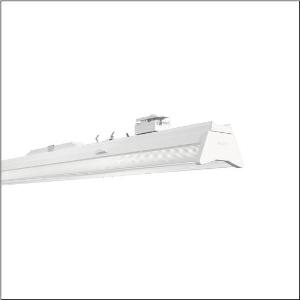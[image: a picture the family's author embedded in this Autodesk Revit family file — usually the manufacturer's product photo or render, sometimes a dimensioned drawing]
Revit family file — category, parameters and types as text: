
# Revit family: licross_r__11_performance_tw_51tm16tnt45x_2116
name_source: partatom
category: Lighting Fixtures
units: mm (PartAtom-declared; Revit-internal decimal feet)

## family parameters
Cut with Voids When Loaded = No
Host = Face
Light Source = No
Part Type = Normal
Room Calculation Point = No
Round Connector Dimension = Use Diameter
Shared = No

## types (1)
- --- (1 x LED 2700 K ... 6500 K, 4700 lm, 28.9 W, 2700K)
    Apparent Load = 29 VA
    CIE Flux Codes = 63 87 95 78 100
    Color Rendering = 80
    Color Temperature = 2700K
    Default Elevation = 1800 mm
    Description = Licross® 11 Performance TW, luminaire insert, of sheet steel, galvanised, coil coated, white, length: 1.500mm, width: 120mm, height: 123mm, LED rated luminous flux: 4.700lm, light colour: 8tw, control gear: DALI DT8, with plug, 5-pole, with phase selection, mains connection: 220..240V, AC, 50/60Hz, rated input power: 28.9W, halogen-free wiring, primary light control with lens, of plastic, primary optical cover: cover, of PMMA, light emission: direct/indirect distribution, primary light characteristic: symmetric, protection rating (complete): IP40, insulation class (complete): insulation class I (protective earthing), certification: CE, ENEC, VDE, UKCA, protection symbol: D if used in an environment without relevant dust loads with corresponding accessories, impact resistance: IK06, permissible ambient temperature for indoor applications: -25..+45°C, corresponds to IFS (International Featured Standards) requirements for safety and quality in the food industry, reducing of maximum allowable ambient temperature of 5°C with ceiling mounting, LABS conformity tested according to VDMA 24364:2018-05, packaging unit: 1 piece
    Height = 114 mm
    Lamp = 1 x LED 2700 K ... 6500 K
    Lamp Light Flux = 4700 lm
    Lamp Power = 28.9 W
    Lamp count = 1
    Length = 1500 mm
    Luminous efficacy = 163 lm/W
    Manufacturer = Siteco
    ModVariant = No
    Model = 51TM16TNT45X
    Mounting Place = Ceiling
    Mounting Type = Pendant
    Number of Poles = 1
    OnlyDefault = Yes
    Power Factor = 1
    Product Name = Licross® 11 Performance TW
    Product group = luminaire insert
    ProductGroupID = 901
    Protection Class = Protection class I
    Protection Degree = IP 40
    RLX_Detail_Level = 1
    RLX_Emergency_Light_Flux = 0 lm
    RLX_Emergency_Type = 0
    RLX_Emergency_Type_DB = No
    RlxData = <blob elided: 30369 chars, md5=9de76e66>
    Socket = socket
    Standby Power = 0 W
    System Light Flux = 4700 lm
    System Power = 29 W
    Type Comments = individual setting: CCT=2700K
    Type Image = l_1256138.jpg
    URL = http://relux.com
    VarID = @adj_016019
    Voltage = 0 V
    Weight = 0.00 kg
    Width = 120 mm

## geometry (parser evidence)
native form markers: Blend x4, Sweep x12
no freeform markers — native parametric forms only
